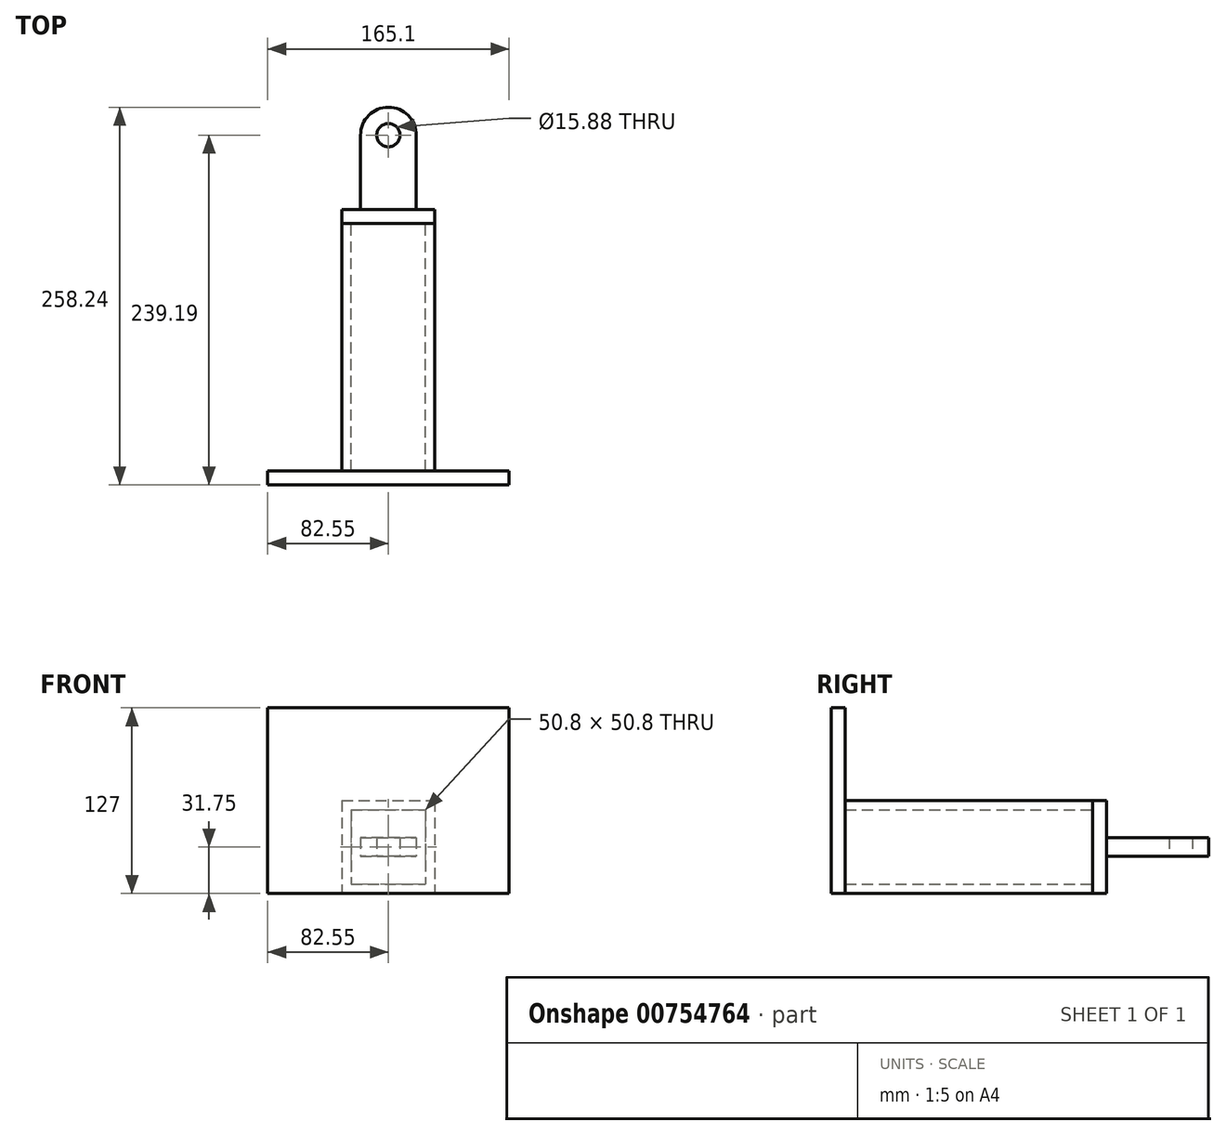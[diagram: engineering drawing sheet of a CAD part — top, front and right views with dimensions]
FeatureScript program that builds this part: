
annotation { "Feature Type Name" : "Feature", "Feature Type Description" : "" }
export const myFeature = defineFeature(function(context is Context, id is Id, definition is map)
    precondition{}
    {
        {
            var Q0;
            Q0=qCreatedBy(makeId("Top.planeOp"),FACE);
            var sketch = newSketch(context, id + "F0", { "sketchPlane" : qUnion([Q0])});
            skArc(sketch, "E0", {"start": v(19.05, 0) * mm, "mid": v(0, 19.05) * mm, "end": v(-19.05, 0) * mm});
            skLineSegment(sketch, "E1.0", {"start": v(-19.05, 0) * mm, "end": v(-19.05, -50.8) * mm});
            skLineSegment(sketch, "E2.0", {"start": v(19.05, 0) * mm, "end": v(19.05, -50.8) * mm});
            skLineSegment(sketch, "E3.0", {"start": v(-19.05, -50.8) * mm, "end": v(19.05, -50.8) * mm});
            skCircle(sketch, "E4", {"center": v(0, 0) * mm, "radius": 7.94 * mm});
            skSolve(sketch);
        }
        {
            var Q0;
            Q0=makeQuery(id+"F0.imprint","IMPRINT",FACE,{"disambiguationData":[TD([[makeQuery(id+"F0.imprint","IMPRINT",EDGE,{"derivedFrom":sQuery(id+"F0.wireOp",EDGE,"E0")}),1.0]])]});
            extrude(context, id + "F1", {"entities" : qUnion([Q0]), "depth" : 6.35 * mm, "offsetDistance" : 25.4 * mm, "hasSecondDirection" : true, "secondDirectionOppositeDirection" : true, "secondDirectionDepth" : 6.35 * mm});
        }
        {
            var Q0;
            Q0=makeQuery(id+"F1.opExtrude","SWEPT_FACE",FACE,{"disambiguationData":[OSD([sQuery(id+"F0.wireOp",EDGE,"E3.0")])]});
            var sketch = newSketch(context, id + "F2", { "sketchPlane" : qUnion([Q0])});
            skLineSegment(sketch, "E5.bottom", {"start": v(-31.75, 31.75) * mm, "end": v(31.75, 31.75) * mm});
            skLineSegment(sketch, "E5.top", {"start": v(-31.75, -31.75) * mm, "end": v(31.75, -31.75) * mm});
            skLineSegment(sketch, "E5.left", {"start": v(-31.75, 31.75) * mm, "end": v(-31.75, -31.75) * mm});
            skLineSegment(sketch, "E5.right", {"start": v(31.75, 31.75) * mm, "end": v(31.75, -31.75) * mm});
            skSolve(sketch);
        }
        {
            var Q0;
            Q0=qSketchRegion(id+"F2",true);
            extrude(context, id + "F3", {"entities" : qUnion([Q0]), "operationType" : NewBodyOperationType.ADD, "depth" : 9.52 * mm, "offsetDistance" : 25.4 * mm});
        }
        {
            var Q0;
            Q0=makeQuery(id+"F3.opExtrude","CAP_FACE",FACE,{"disambiguationData":[OSD([sQuery(id+"F2.wireOp",EDGE,"E5.bottom"),sQuery(id+"F2.wireOp",EDGE,"E5.top"),sQuery(id+"F2.wireOp",EDGE,"E5.left"),sQuery(id+"F2.wireOp",EDGE,"E5.right")])],"isStart":false});
            var sketch = newSketch(context, id + "F4", { "sketchPlane" : qUnion([Q0])});
            skLineSegment(sketch, "E6.bottom", {"start": v(-31.75, 31.75) * mm, "end": v(31.75, 31.75) * mm});
            skLineSegment(sketch, "E6.top", {"start": v(-31.75, -31.75) * mm, "end": v(31.75, -31.75) * mm});
            skLineSegment(sketch, "E6.left", {"start": v(-31.75, 31.75) * mm, "end": v(-31.75, -31.75) * mm});
            skLineSegment(sketch, "E6.right", {"start": v(31.75, 31.75) * mm, "end": v(31.75, -31.75) * mm});
            skLineSegment(sketch, "E7.0", {"start": v(-25.4, 25.4) * mm, "end": v(25.4, 25.4) * mm});
            skLineSegment(sketch, "E7.1", {"start": v(-25.4, 25.4) * mm, "end": v(-25.4, -25.4) * mm});
            skLineSegment(sketch, "E7.2", {"start": v(-25.4, -25.4) * mm, "end": v(25.4, -25.4) * mm});
            skLineSegment(sketch, "E7.3", {"start": v(25.4, 25.4) * mm, "end": v(25.4, -25.4) * mm});
            skSolve(sketch);
        }
        {
            var Q0;
            Q0=qSketchRegion(id+"F4",true);
            extrude(context, id + "F5", {"entities" : qUnion([Q0]), "depth" : 169.34 * mm, "offsetDistance" : 25.4 * mm});
        }
        {
            var Q0;
            Q0=makeQuery(id+"F5.opExtrude","CAP_FACE",FACE,{"disambiguationData":[OSD([sQuery(id+"F4.wireOp",EDGE,"E6.bottom"),sQuery(id+"F4.wireOp",EDGE,"E6.top"),sQuery(id+"F4.wireOp",EDGE,"E6.left"),sQuery(id+"F4.wireOp",EDGE,"E6.right"),sQuery(id+"F4.wireOp",EDGE,"E7.0"),sQuery(id+"F4.wireOp",EDGE,"E7.1"),sQuery(id+"F4.wireOp",EDGE,"E7.2"),sQuery(id+"F4.wireOp",EDGE,"E7.3")])],"isStart":false});
            var sketch = newSketch(context, id + "F6", { "sketchPlane" : qUnion([Q0])});
            skLineSegment(sketch, "E8.bottom", {"start": v(-82.55, -31.75) * mm, "end": v(82.55, -31.75) * mm});
            skLineSegment(sketch, "E8.top", {"start": v(-82.55, 95.25) * mm, "end": v(82.55, 95.25) * mm});
            skLineSegment(sketch, "E8.left", {"start": v(-82.55, -31.75) * mm, "end": v(-82.55, 95.25) * mm});
            skLineSegment(sketch, "E8.right", {"start": v(82.55, -31.75) * mm, "end": v(82.55, 95.25) * mm});
            skSolve(sketch);
        }
        {
            var Q0;
            Q0=qSketchRegion(id+"F6",true);
            extrude(context, id + "F7", {"entities" : qUnion([Q0]), "depth" : 9.52 * mm, "offsetDistance" : 25.4 * mm});
        }
    });
